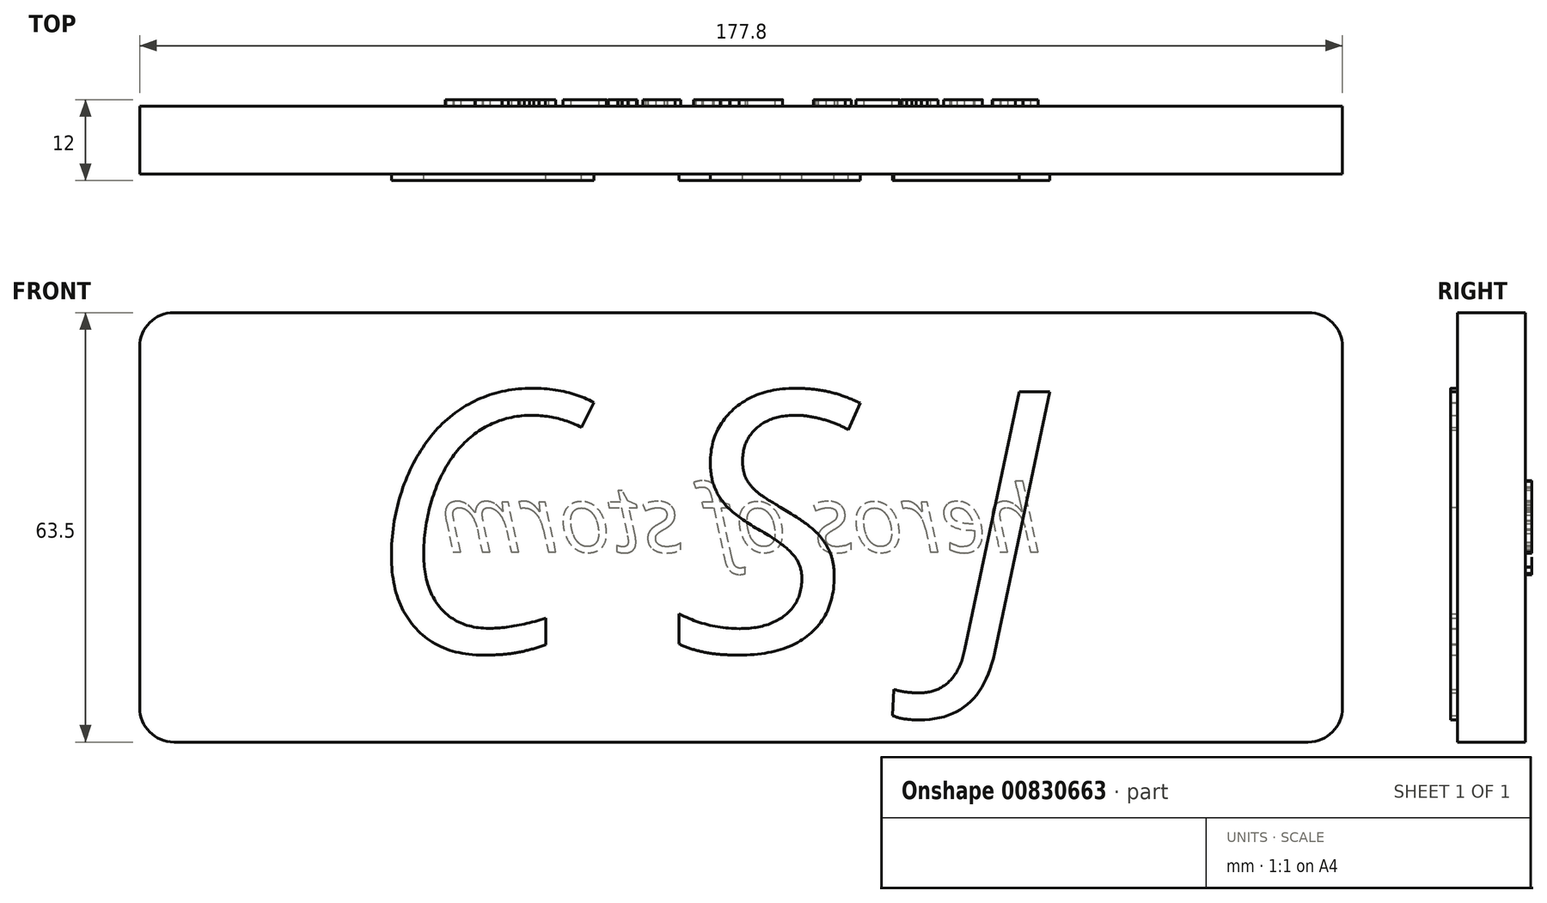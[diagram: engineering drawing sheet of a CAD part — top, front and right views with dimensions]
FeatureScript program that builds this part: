
annotation { "Feature Type Name" : "Feature", "Feature Type Description" : "" }
export const myFeature = defineFeature(function(context is Context, id is Id, definition is map)
    precondition{}
    {
        {
            var Q0;
            Q0=qCreatedBy(makeId("Front.planeOp"),FACE);
            var sketch = newSketch(context, id + "F0", { "sketchPlane" : qUnion([Q0])});
            skLineSegment(sketch, "E0.bottom", {"start": v(-88.9, 31.75) * mm, "end": v(88.9, 31.75) * mm});
            skLineSegment(sketch, "E0.top", {"start": v(-88.9, -31.75) * mm, "end": v(88.9, -31.75) * mm});
            skLineSegment(sketch, "E0.left", {"start": v(-88.9, 31.75) * mm, "end": v(-88.9, -31.75) * mm});
            skLineSegment(sketch, "E0.right", {"start": v(88.9, 31.75) * mm, "end": v(88.9, -31.75) * mm});
            skPoint(sketch, "E0.middle", {"position": v(0, 0) * mm});
            skSolve(sketch);
        }
        {
            var Q0;
            Q0=makeQuery(id+"F0.imprint","IMPRINT",FACE,{"disambiguationData":[TD([[makeQuery(id+"F0.imprint","IMPRINT",EDGE,{"derivedFrom":sQuery(id+"F0.wireOp",EDGE,"E0.bottom")}),-1.0]])]});
            extrude(context, id + "F1", {"entities" : qUnion([Q0]), "depth" : 10 * mm, "offsetDistance" : 25.4 * mm});
        }
        {
            var Q0;
            Q0=makeQuery(id+"F1.opExtrude","SWEPT_EDGE",EDGE,{"disambiguationData":[OSD([sQuery(id+"F0.wireOp",EDGE,"E0.bottom"),sQuery(id+"F0.wireOp",EDGE,"E0.right")])]});
            var Q1;
            Q1=makeQuery(id+"F1.opExtrude","SWEPT_EDGE",EDGE,{"disambiguationData":[OSD([sQuery(id+"F0.wireOp",EDGE,"E0.top"),sQuery(id+"F0.wireOp",EDGE,"E0.right")])]});
            var Q2;
            Q2=makeQuery(id+"F1.opExtrude","SWEPT_EDGE",EDGE,{"disambiguationData":[OSD([sQuery(id+"F0.wireOp",EDGE,"E0.top"),sQuery(id+"F0.wireOp",EDGE,"E0.left")])]});
            var Q3;
            Q3=makeQuery(id+"F1.opExtrude","SWEPT_EDGE",EDGE,{"disambiguationData":[OSD([sQuery(id+"F0.wireOp",EDGE,"E0.bottom"),sQuery(id+"F0.wireOp",EDGE,"E0.left")])]});
            fillet(context, id + "F2", {"entities" : qUnion([Q0, Q1, Q2, Q3]), "radius" : 5.08 * mm, "tangentPropagation" : true, "allowEdgeOverflow" : false});
        }
        {
            var Q0;
            Q0=makeQuery(id+"F1.opExtrude","CAP_FACE",FACE,{"disambiguationData":[OSD([sQuery(id+"F0.wireOp",EDGE,"E0.bottom"),sQuery(id+"F0.wireOp",EDGE,"E0.top"),sQuery(id+"F0.wireOp",EDGE,"E0.left"),sQuery(id+"F0.wireOp",EDGE,"E0.right")])],"isStart":false});
            var sketch = newSketch(context, id + "F3", { "sketchPlane" : qUnion([Q0])});
            skText(sketch, "E1", { "text": "C S J", "fontName": "OpenSans-Italic.ttf"});
            const initialGuessF3  = {"E1": [-0.05562, -0.01837, 1, 0, 0.03871]};
            skSetInitialGuess(sketch, initialGuessF3);
            skSolve(sketch);
        }
        {
            var Q0;
            Q0 = qSketchRegion(id + "F3", true);
            extrude(context, id + "F4", {"entities" : qUnion([Q0]), "operationType" : NewBodyOperationType.ADD, "depth" : 1 * mm, "offsetDistance" : 25.4 * mm});
        }
        {
            var Q0;
            Q0=makeQuery(id+"F1.opExtrude","CAP_FACE",FACE,{"disambiguationData":[OSD([sQuery(id+"F0.wireOp",EDGE,"E0.bottom"),sQuery(id+"F0.wireOp",EDGE,"E0.top"),sQuery(id+"F0.wireOp",EDGE,"E0.left"),sQuery(id+"F0.wireOp",EDGE,"E0.right")])],"isStart":true});
            var sketch = newSketch(context, id + "F5", { "sketchPlane" : qUnion([Q0])});
            skText(sketch, "E2", { "text": "heros of storm", "fontName": "OpenSans-Italic.ttf"});
            const initialGuessF5  = {"E2": [-0.0443, -0.00367, 1, 0, 0.00994]};
            skSetInitialGuess(sketch, initialGuessF5);
            skSolve(sketch);
        }
        {
            var Q0;
            Q0 = qSketchRegion(id + "F5", true);
            extrude(context, id + "F6", {"entities" : qUnion([Q0]), "operationType" : NewBodyOperationType.ADD, "depth" : 1 * mm, "offsetDistance" : 25.4 * mm});
        }
    });
